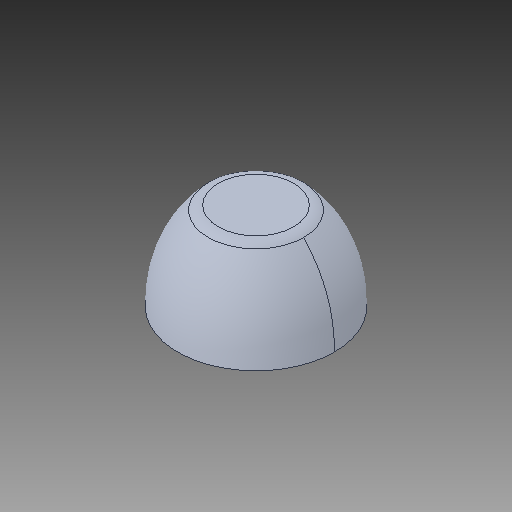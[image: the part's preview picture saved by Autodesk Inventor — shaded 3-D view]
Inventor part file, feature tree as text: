
AUTODESK INVENTOR PART (.ipt)
format: ipt  version: 2018.3 (Build 223284000, 284)  size: 136,704 bytes
history: native  units: mm
features: other x1, fillet x1
ambient origin geometry x8: Origin, YZ Plane, XZ Plane, XY Plane, X Axis, Y Axis, Z Axis, Center Point
bodies: Body1 (feature_tree)
feature tree (2):
  other  "Sólido1"
  fillet  "Fillet1"  [1 undecoded]
note: 1 required parameter value undecoded (feature->parameter linkage not recoverable at this tier; creation-order binding heuristic only, values carry confidence <= 0.55)
